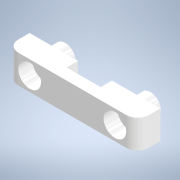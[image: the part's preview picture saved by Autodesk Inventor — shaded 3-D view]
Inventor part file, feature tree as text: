
AUTODESK INVENTOR PART (.ipt)
format: ipt  version: 2020 (Build 240168000, 168)  size: 152,576 bytes
history: native  units: mm
features: extrude x5, other x1, sketch x1, fillet x1
ambient origin geometry x8: Origin, YZ Plane, XZ Plane, XY Plane, X Axis, Y Axis, Z Axis, Center Point
bodies: Body1 (feature_tree)
feature tree (8):
  other  "Bryła1"
  sketch  "Szkic1"
  extrude  "Wyciągnięcie proste1"  Depth=10.0mm
  extrude  "Wyciągnięcie proste2"  Depth=7.5mm
  extrude  "Wyciągnięcie proste3"  Depth=4.5mm
  extrude  "Wyciągnięcie proste4"  Depth=15.0mm
  extrude  "Wyciągnięcie proste5"  Depth=15.0mm
  fillet  "Zaokrąglenie1"  Radius=8.0mm
